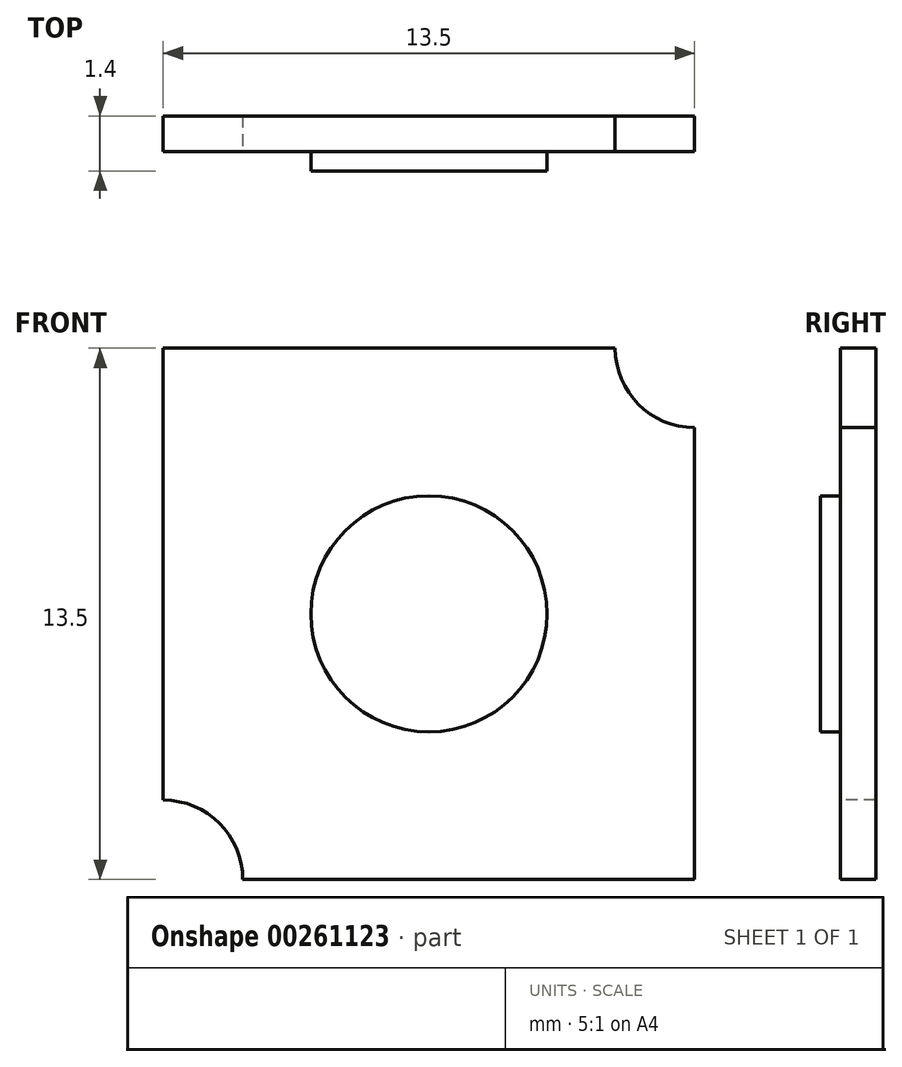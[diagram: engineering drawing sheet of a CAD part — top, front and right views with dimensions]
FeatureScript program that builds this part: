
annotation { "Feature Type Name" : "Feature", "Feature Type Description" : "" }
export const myFeature = defineFeature(function(context is Context, id is Id, definition is map)
    precondition{}
    {
        {
            var Q0;
            Q0=qCreatedBy(makeId("Front.planeOp"),FACE);
            var sketch = newSketch(context, id + "F0", { "sketchPlane" : qUnion([Q0])});
            skLineSegment(sketch, "E0.bottom", {"start": v(6.75, 6.75) * mm, "end": v(-6.75, 6.75) * mm});
            skLineSegment(sketch, "E0.top", {"start": v(6.75, -6.75) * mm, "end": v(-6.75, -6.75) * mm});
            skLineSegment(sketch, "E0.left", {"start": v(6.75, 6.75) * mm, "end": v(6.75, -6.75) * mm});
            skLineSegment(sketch, "E0.right", {"start": v(-6.75, 6.75) * mm, "end": v(-6.75, -6.75) * mm});
            skPoint(sketch, "E0.middle", {"position": v(0, 0) * mm});
            skCircle(sketch, "E1", {"center": v(0, 0) * mm, "radius": 3 * mm});
            skSolve(sketch);
        }
        {
            var Q0;
            Q0=makeQuery(id+"F0.imprint","IMPRINT",FACE,{"disambiguationData":[TD([[makeQuery(id+"F0.imprint","IMPRINT",EDGE,{"derivedFrom":sQuery(id+"F0.wireOp",EDGE,"E1")}),1.0]])]});
            extrude(context, id + "F1", {"entities" : qUnion([Q0]), "depth" : 1.4 * mm});
        }
        {
            var Q0;
            Q0 = qSketchRegion(id + "F0", true);
            extrude(context, id + "F2", {"entities" : qUnion([Q0]), "operationType" : NewBodyOperationType.ADD, "depth" : 0.9 * mm});
        }
        {
            var Q0;
            Q0=makeQuery(id+"F2.opExtrude","CAP_FACE",FACE,{"disambiguationData":[OSD([sQuery(id+"F0.wireOp",EDGE,"E0.bottom"),sQuery(id+"F0.wireOp",EDGE,"E0.top"),sQuery(id+"F0.wireOp",EDGE,"E0.left"),sQuery(id+"F0.wireOp",EDGE,"E0.right"),sQuery(id+"F0.wireOp",EDGE,"E1")])],"isStart":false});
            var sketch = newSketch(context, id + "F3", { "sketchPlane" : qUnion([Q0])});
            skCircle(sketch, "E2", {"center": v(6.75, 6.75) * mm, "radius": 2.02 * mm});
            skCircle(sketch, "E3", {"center": v(-6.75, -6.75) * mm, "radius": 2.02 * mm});
            skLineSegment(sketch, "E4", {"start": v(-6.75, 6.75) * mm, "end": v(4.73, 6.75) * mm});
            skSolve(sketch);
        }
        {
            var Q0;
            {var subQ1=makeQuery(id+"F2.opExtrude","CAP_EDGE",EDGE,{"disambiguationData":[OSD([sQuery(id+"F0.wireOp",EDGE,"E0.bottom")])],"isStart":false});var subQ3=makeQuery(id+"F2.opExtrude","CAP_EDGE",EDGE,{"disambiguationData":[OSD([sQuery(id+"F0.wireOp",EDGE,"E0.left")])],"isStart":false});var subQ5=makeQuery(id+"F3.imprint","INTERSECT",VERTEX,{"derivedFrom":[subQ1,subQ3]});Q0=makeQuery(id+"F3.imprint","IMPRINT",FACE,{"disambiguationData":[TD([[makeQuery(id+"F3.imprint","IMPRINT",EDGE,{"disambiguationData":[TD([[subQ5,-1.0]])],"derivedFrom":subQ3}),1.0]])]});}
            var Q1;
            {var subQ1=makeQuery(id+"F2.opExtrude","CAP_EDGE",EDGE,{"disambiguationData":[OSD([sQuery(id+"F0.wireOp",EDGE,"E0.bottom")])],"isStart":false});var subQ3=makeQuery(id+"F2.opExtrude","CAP_EDGE",EDGE,{"disambiguationData":[OSD([sQuery(id+"F0.wireOp",EDGE,"E0.left")])],"isStart":false});var subQ5=makeQuery(id+"F3.imprint","INTERSECT",VERTEX,{"derivedFrom":[subQ1,subQ3]});Q1=makeQuery(id+"F3.imprint","IMPRINT",FACE,{"disambiguationData":[TD([[makeQuery(id+"F3.imprint","IMPRINT",EDGE,{"disambiguationData":[TD([[subQ5,-1.0]])],"derivedFrom":subQ3}),-1.0]])]});}
            var Q2;
            {var subQ0=sQuery(id+"F3.wireOp",EDGE,"E3");var subQ1=makeQuery(id+"F2.opExtrude","CAP_EDGE",EDGE,{"disambiguationData":[OSD([sQuery(id+"F0.wireOp",EDGE,"E0.top")])],"isStart":false});var subQ2=makeQuery(id+"F3.imprint","INTERSECT",VERTEX,{"derivedFrom":[subQ1,subQ0]});Q2=makeQuery(id+"F3.imprint","IMPRINT",FACE,{"disambiguationData":[TD([[makeQuery(id+"F3.imprint","IMPRINT",EDGE,{"disambiguationData":[TD([[subQ2,-1.0]])],"derivedFrom":subQ0}),1.0]])]});}
            var Q3;
            {var subQ0=sQuery(id+"F3.wireOp",EDGE,"E3");var subQ1=makeQuery(id+"F2.opExtrude","CAP_EDGE",EDGE,{"disambiguationData":[OSD([sQuery(id+"F0.wireOp",EDGE,"E0.top")])],"isStart":false});var subQ2=makeQuery(id+"F3.imprint","INTERSECT",VERTEX,{"derivedFrom":[subQ1,subQ0]});Q3=makeQuery(id+"F3.imprint","IMPRINT",FACE,{"disambiguationData":[TD([[makeQuery(id+"F3.imprint","IMPRINT",EDGE,{"disambiguationData":[TD([[subQ2,1.0]])],"derivedFrom":subQ0}),1.0]])]});}
            extrude(context, id + "F4", {"entities" : qUnion([Q0, Q1, Q2, Q3]), "operationType" : NewBodyOperationType.REMOVE, "oppositeDirection" : true, "depth" : 25 * mm});
        }
    });
